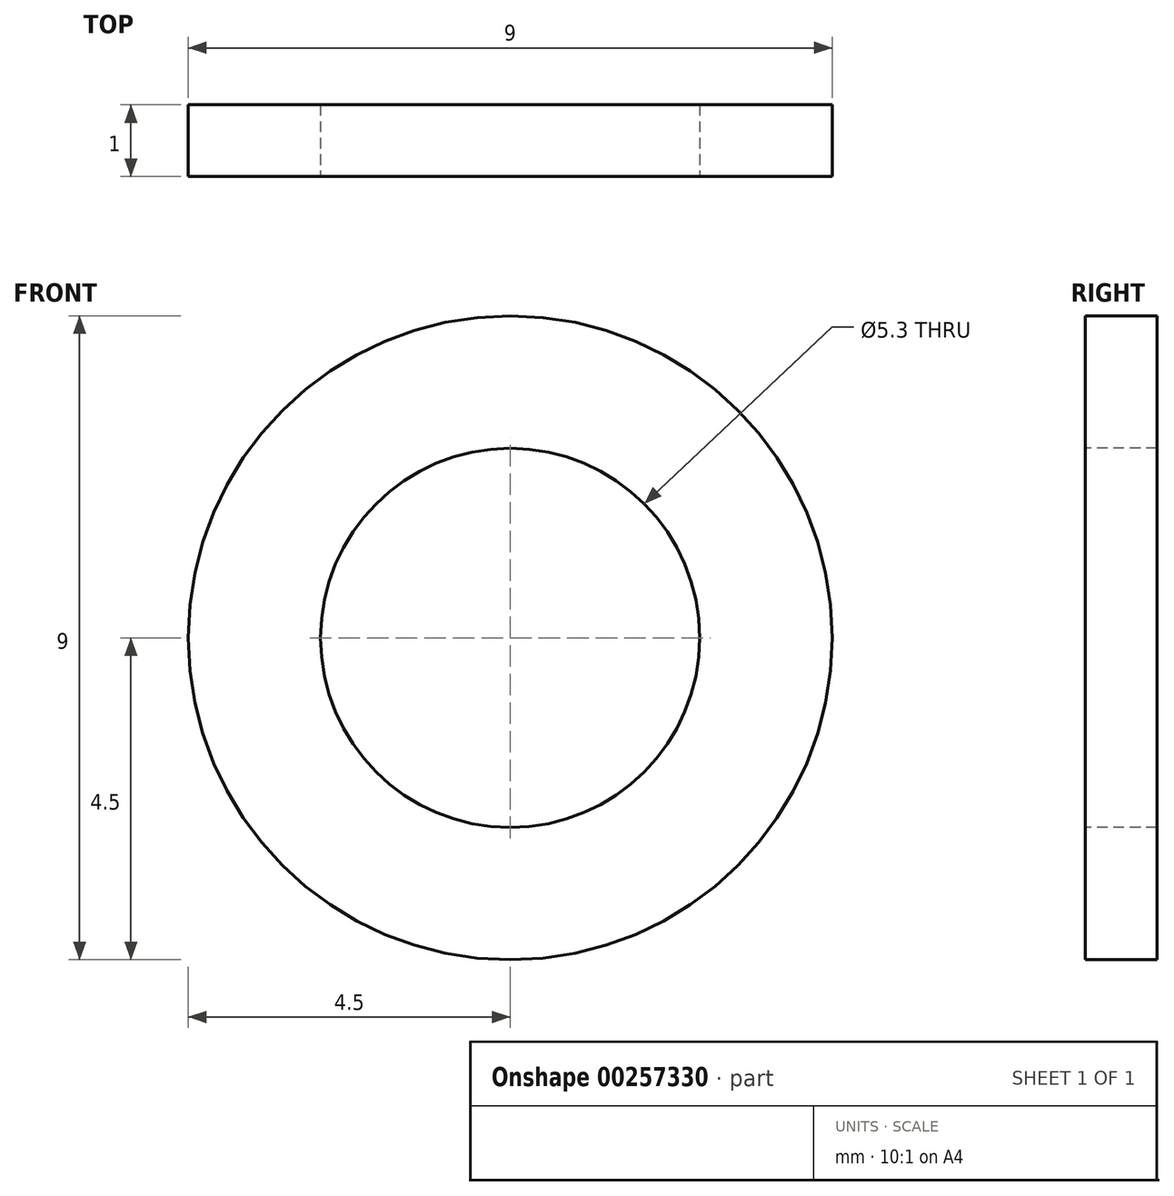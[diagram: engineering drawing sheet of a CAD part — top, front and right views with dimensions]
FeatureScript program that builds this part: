
annotation { "Feature Type Name" : "Feature", "Feature Type Description" : "" }
export const myFeature = defineFeature(function(context is Context, id is Id, definition is map)
    precondition{}
    {
        {
            var Q0;
            Q0=qCreatedBy(makeId("Right.planeOp"),FACE);
            var sketch = newSketch(context, id + "F0", { "sketchPlane" : qUnion([Q0])});
            skLineSegment(sketch, "E0", {"start": v(-4.49, 0) * mm, "end": v(5.72, 0) * mm, "construction": true});
            skLineSegment(sketch, "E1.bottom", {"start": v(0, 4.5) * mm, "end": v(1, 4.5) * mm});
            skLineSegment(sketch, "E1.top", {"start": v(0, 2.65) * mm, "end": v(1, 2.65) * mm});
            skLineSegment(sketch, "E1.left", {"start": v(0, 4.5) * mm, "end": v(0, 2.65) * mm});
            skLineSegment(sketch, "E1.right", {"start": v(1, 4.5) * mm, "end": v(1, 2.65) * mm});
            skSolve(sketch);
        }
        {
            var Q0;
            Q0=makeQuery(id+"F0.imprint","IMPRINT",FACE,{"disambiguationData":[TD([[makeQuery(id+"F0.imprint","IMPRINT",EDGE,{"derivedFrom":sQuery(id+"F0.wireOp",EDGE,"E1.bottom")}),-1.0]])]});
            var Q1;
            Q1=sQuery(id+"F0.wireOp",EDGE,"E0");
            revolve(context, id + "F1", {"entities" : qUnion([Q0]), "axis" : qUnion([Q1]), "revolveType" : RevolveType.FULL});
        }
    });
